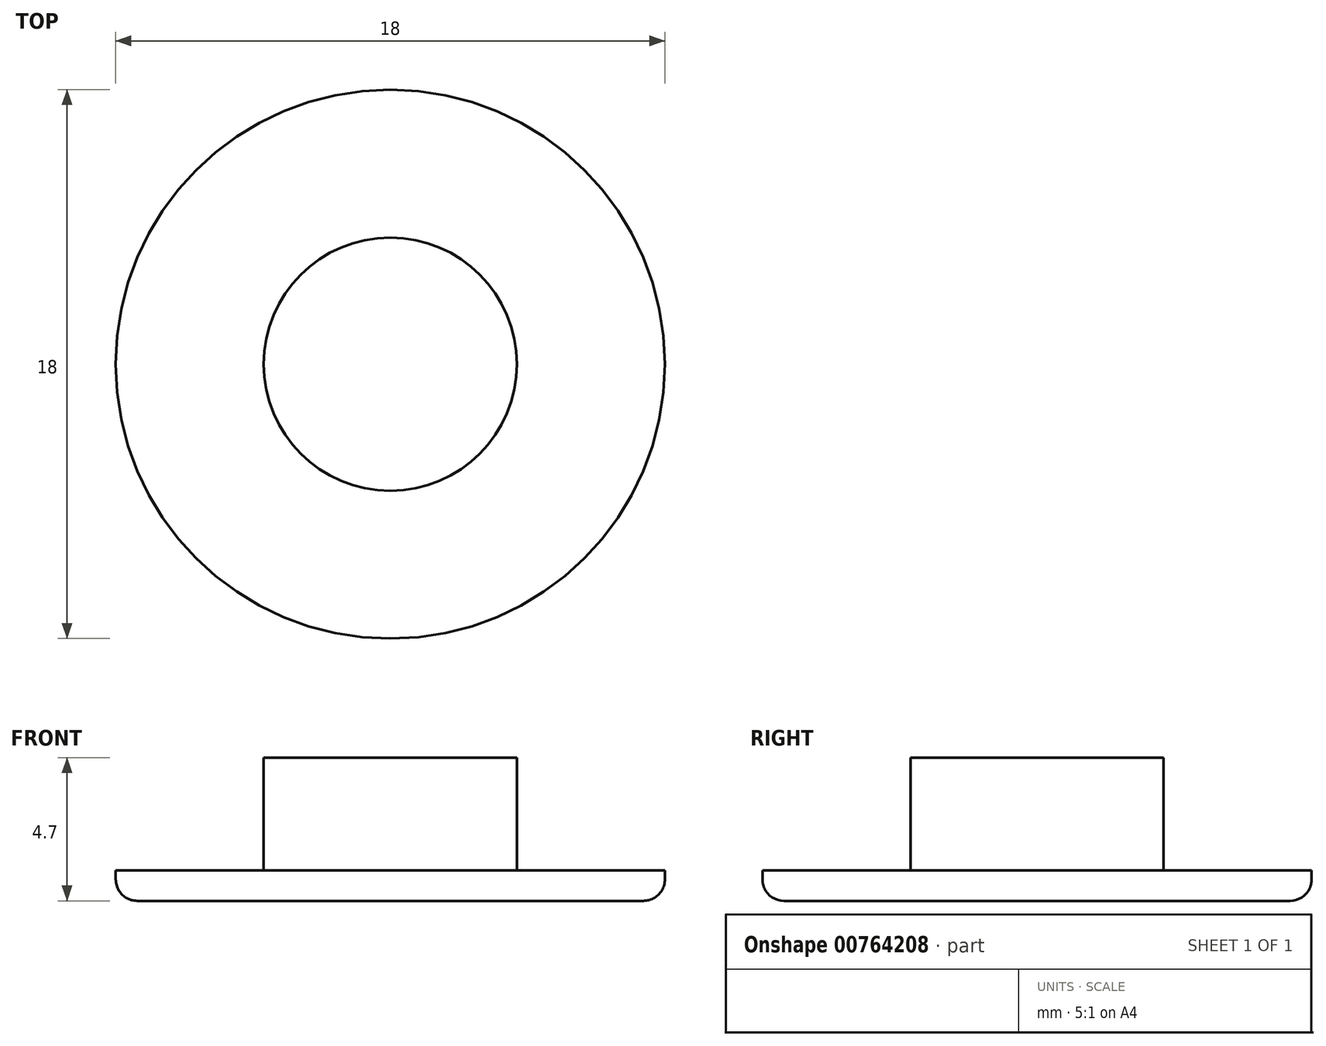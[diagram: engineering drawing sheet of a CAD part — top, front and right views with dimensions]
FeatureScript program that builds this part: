
annotation { "Feature Type Name" : "Feature", "Feature Type Description" : "" }
export const myFeature = defineFeature(function(context is Context, id is Id, definition is map)
    precondition{}
    {
        {
            var Q0;
            Q0=qCreatedBy(makeId("Top.planeOp"),FACE);
            var sketch = newSketch(context, id + "F0", { "sketchPlane" : qUnion([Q0])});
            skCircle(sketch, "E0", {"center": v(0, 0) * mm, "radius": 9 * mm});
            skSolve(sketch);
        }
        {
            var Q0;
            Q0 = qSketchRegion(id + "F0", true);
            extrude(context, id + "F1", {"entities" : qUnion([Q0]), "depth" : 1 * mm, "offsetDistance" : 25 * mm});
        }
        {
            var Q0;
            Q0=makeQuery(id+"F1.opExtrude","CAP_FACE",FACE,{"disambiguationData":[OSD([sQuery(id+"F0.wireOp",EDGE,"E0")])],"isStart":false});
            var sketch = newSketch(context, id + "F2", { "sketchPlane" : qUnion([Q0])});
            skCircle(sketch, "E1", {"center": v(0, 0) * mm, "radius": 4.15 * mm});
            skSolve(sketch);
        }
        {
            var Q0;
            Q0 = qSketchRegion(id + "F2", true);
            extrude(context, id + "F3", {"entities" : qUnion([Q0]), "operationType" : NewBodyOperationType.ADD, "depth" : 3.7 * mm, "offsetDistance" : 25 * mm});
        }
        {
            var Q0;
            Q0=makeQuery(id+"F1.opExtrude","CAP_EDGE",EDGE,{"disambiguationData":[OSD([sQuery(id+"F0.wireOp",EDGE,"E0")])],"isStart":true});
            fillet(context, id + "F4", {"entities" : qUnion([Q0]), "radius" : .7 * mm, "tangentPropagation" : true, "allowEdgeOverflow" : false});
        }
    });
